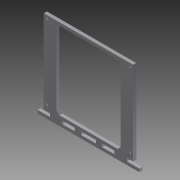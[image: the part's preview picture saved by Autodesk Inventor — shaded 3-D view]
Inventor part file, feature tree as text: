
AUTODESK INVENTOR PART (.ipt)
format: ipt  version: 2011 (Build 150239000, 239)  size: 667,648 bytes
history: native  units: in
note: dims shown in document units (in); Inventor stores cm internally (conversion verified against a paired STEP export)
features: extrude x24, sketch x24, fillet x2
ambient origin geometry x8: Origin, YZ Plane, XZ Plane, XY Plane, X Axis, Y Axis, Z Axis, Center Point
bodies: Solid1 (feature_tree)
feature tree (50):
  extrude  "Extrusion1"  Depth=41.5in
  extrude  "Extrusion2"  Depth=10.0in
  extrude  "Extrusion3"  Depth=0.6in
  extrude  "Extrusion4"  Depth=0.25in
  extrude  "Extrusion5"  Depth=0.5in
  extrude  "Extrusion6"  Depth=1.0in
  extrude  "Extrusion7"  Depth=4.1in TaperAngle=0.0deg
  extrude  "Extrusion8"  Depth=1.0in
  extrude  "Extrusion9"  Depth=1.0in
  extrude  "Extrusion10"  Depth=1.0in
  extrude  "Extrusion11"  Depth=4.1in TaperAngle=0.0deg
  extrude  "Extrusion12"  Depth=0.5in
  fillet  "Fillet1"  Radius=0.25in
  fillet  "Fillet2"  Radius=1.0in
  extrude  "Extrusion13"  Depth=3.0in
  extrude  "Extrusion14"  Depth=3.0in
  extrude  "Extrusion15"  Depth=3.0in
  extrude  "Extrusion16"  Depth=3.0in
  extrude  "Extrusion17"  Depth=3.0in
  extrude  "Extrusion18"  Depth=0.25in
  extrude  "Extrusion19"  Depth=0.25in TaperAngle=0.0deg
  extrude  "Extrusion20"  Depth=0.25in
  extrude  "Extrusion21"  Depth=1.0in
  extrude  "Extrusion22"  Depth=1.0in
  extrude  "Extrusion23"  Depth=0.156in
  extrude  "Extrusion24"  Depth=0.156in
  sketch  "Sketch1"  dims[d0=20.0in d1=41.5in]
  sketch  "Sketch2"  dims[d2=0.25in d3=0.0in d4=10.0in]
  sketch  "Sketch3"  dims[d5=0.25in d6=0.6in]
  sketch  "Sketch4"  dims[d7=1.2in d8=0.25in]
  sketch  "Sketch5"  dims[d9=4.1in d10=0.0in d11=0.5in]
  sketch  "Sketch6"  dims[d12=0.5in d13=1.0in]
  sketch  "Sketch7"  dims[d14=1.0in d15=4.1in d16=0.0in]
  sketch  "Sketch8"  dims[d17=1.0in d18=1.0in]
  sketch  "Sketch9"  dims[d19=1.0in d20=1.0in]
  sketch  "Sketch10"  dims[d21=6.75in d22=1.0in]
  sketch  "Sketch11"  dims[d23=0.5in d24=4.1in d25=0.0in]
  sketch  "Sketch12"  dims[d26=0.25in d27=0.5in d28=0.25in d29=0.0in d30=1.0in]
  sketch  "Sketch13"  dims[d31=1.0in d32=3.0in]
  sketch  "Sketch14"  dims[d33=1.0in d34=3.0in]
  sketch  "Sketch15"  dims[d35=1.0in d36=3.0in]
  sketch  "Sketch16"  dims[d37=1.0in d38=3.0in]
  sketch  "Sketch17"  dims[d39=1.0in d40=3.0in]
  sketch  "Sketch18"  dims[d41=1.0in d42=0.25in]
  sketch  "Sketch19"  dims[d43=1.0in d44=0.0in d45=0.25in d46=0.0in]
  sketch  "Sketch20"  dims[d47=1.0in d48=0.25in]
  sketch  "Sketch21"  dims[d49=1.0in d50=1.0in]
  sketch  "Sketch22"  dims[d51=1.0in d52=1.0in]
  sketch  "Sketch23"  dims[d53=0.25in d54=0.0in d55=0.156in]
  sketch  "Sketch24"  dims[d56=0.156in d57=0.156in d58=0.156in d59=0.25in d60=0.0in d61=0.25in d62=0.0in d63=0.25in d64=0.0in d65=1.0in d66=1.0in d67=1.0in d68=1.0in d69=1.0in d70=1.0in d71=1.0in d72=1.0in d73=0.25in d74=0.0in d75=0.5in d76=0.5in d77=1.0in d78=0.0in d79=3.0in d80=3.0in d81=0.25in d82=0.0in d83=0.75in d84=0.75in d85=0.75in d86=0.75in d87=0.156in d88=0.156in d89=0.25in d90=0.0in d91=0.25in d92=1.0in d93=1.0in d94=1.0in d95=0.25in d96=0.0in d97=0.25in d98=1.0in d99=1.0in d100=1.0in d101=0.25in d102=0.0in d103=1.0in d104=0.0in d105=0.75in d106=0.5in d107=0.156in d108=0.156in d109=1.0in d110=0.0in d111=0.25in d112=0.0in d113=0.5in d114=0.5in d115=1.0in d116=0.25in d117=1.0in d118=1.0in d119=1.0in d120=1.0in d121=1.0in d122=1.0in d123=1.0in d124=1.0in d125=1.0in d126=1.0in d127=1.0in d128=1.0in d129=1.0in d130=1.0in d131=1.0in d132=1.0in d133=1.0in d134=1.0in d135=0.25in d136=0.0in d137=0.25in d138=0.0in d139=1.0in d140=0.0in d141=1.0in d142=0.0in]
